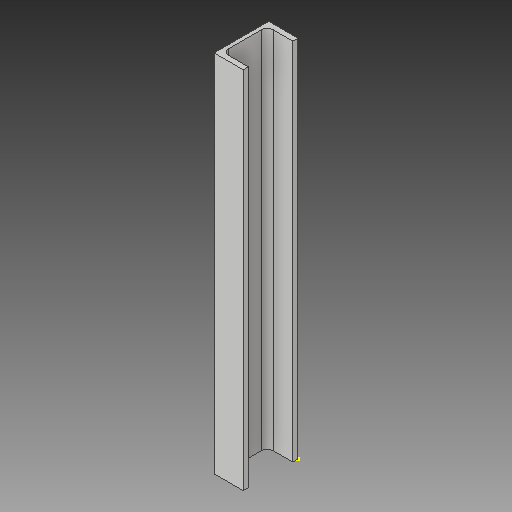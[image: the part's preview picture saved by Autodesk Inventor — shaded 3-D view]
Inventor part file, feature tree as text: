
AUTODESK INVENTOR PART (.ipt)
format: ipt  version: 2019 (Build 230136000, 136)  size: 96,768 bytes
history: native  units: in
note: dims shown in document units (in); Inventor stores cm internally (conversion verified against a paired STEP export)
features: other x3, sketch x2
ambient origin geometry x8: Origin, YZ Plane, XZ Plane, XY Plane, X Axis, Y Axis, Z Axis, Center Point
bodies: Solid1 (feature_tree)
feature tree (5):
  other  "Channel2.ipt"
  other  "Solid1::Channel2.ipt"
  other  "TaggingFeature1"
  sketch  "Sketch1"  dims[d0=0.3937in]
  sketch  "Sketch2"
